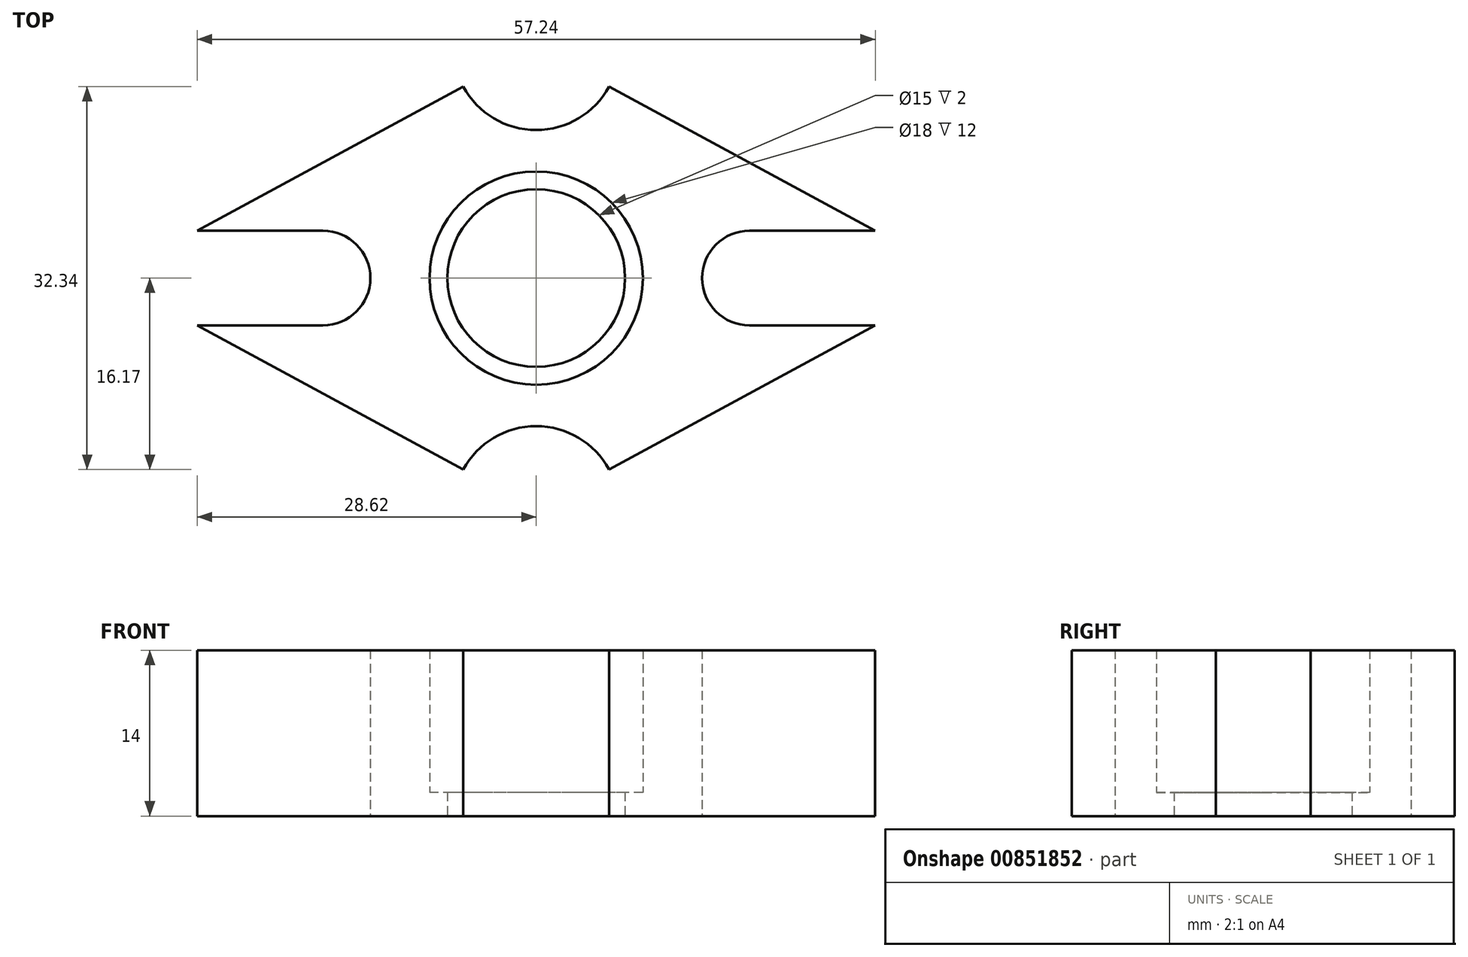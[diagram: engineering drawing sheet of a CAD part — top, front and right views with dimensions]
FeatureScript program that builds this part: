
annotation { "Feature Type Name" : "Feature", "Feature Type Description" : "" }
export const myFeature = defineFeature(function(context is Context, id is Id, definition is map)
    precondition{}
    {
        {
            var Q0;
            Q0=qCreatedBy(makeId("Top.planeOp"),FACE);
            var sketch = newSketch(context, id + "F0", { "sketchPlane" : qUnion([Q0])});
            skPoint(sketch, "E0.middle", {"position": v(0, 0) * mm});
            skCircle(sketch, "E1", {"center": v(0, 0) * mm, "radius": 7.5 * mm});
            skLineSegment(sketch, "E2", {"start": v(-6.16, 16.17) * mm, "end": v(-28.62, 4) * mm});
            skLineSegment(sketch, "E3", {"start": v(-28.62, -4) * mm, "end": v(-6.16, -16.17) * mm});
            skLineSegment(sketch, "E4", {"start": v(6.16, -16.17) * mm, "end": v(28.62, -4) * mm});
            skLineSegment(sketch, "E5", {"start": v(28.62, 4) * mm, "end": v(6.16, 16.17) * mm});
            skArc(sketch, "E6", {"start": v(-6.16, 16.17) * mm, "mid": v(0, 12.5) * mm, "end": v(6.16, 16.17) * mm});
            skArc(sketch, "E7", {"start": v(6.16, -16.17) * mm, "mid": v(0, -12.5) * mm, "end": v(-6.16, -16.17) * mm});
            skPoint(sketch, "E8.endSnap0", {"position": v(-18, 9.75) * mm});
            skPoint(sketch, "E9.orphan", {"position": v(36, -19.5) * mm});
            skPoint(sketch, "E10.orphan", {"position": v(-36, -19.5) * mm});
            skPoint(sketch, "E0.right.end.orphan", {"position": v(-36, 19.5) * mm});
            skPoint(sketch, "E0.left.end.orphan", {"position": v(36, 19.5) * mm});
            skArc(sketch, "E11.0.endCap", {"start": v(-18, 4) * mm, "mid": v(-14, 0) * mm, "end": v(-18, -4) * mm});
            skLineSegment(sketch, "E11.0.left", {"start": v(-28.62, 4) * mm, "end": v(-18, 4) * mm});
            skLineSegment(sketch, "E11.0.right", {"start": v(-28.62, -4) * mm, "end": v(-18, -4) * mm});
            skArc(sketch, "E11.1.endCap", {"start": v(18, -4) * mm, "mid": v(14, 0) * mm, "end": v(18, 4) * mm});
            skLineSegment(sketch, "E11.1.left", {"start": v(28.62, -4) * mm, "end": v(18, -4) * mm});
            skLineSegment(sketch, "E11.1.right", {"start": v(28.62, 4) * mm, "end": v(18, 4) * mm});
            skPoint(sketch, "E11.1.startCap.center.orphan", {"position": v(36, 0) * mm});
            skPoint(sketch, "E12.orphan", {"position": v(-36, 0) * mm});
            skCircle(sketch, "E13", {"center": v(0, 0) * mm, "radius": 9 * mm});
            skSolve(sketch);
        }
        {
            var Q0;
            Q0 = qSketchRegion(id + "F0", true);
            extrude(context, id + "F1", {"entities" : qUnion([Q0]), "depth" : 12 * mm, "offsetDistance" : 25 * mm});
        }
        {
            var Q0;
            Q0=makeQuery(id+"F1.opExtrude","CAP_FACE",FACE,{"disambiguationData":[OSD([sQuery(id+"F0.wireOp",EDGE,"E2"),sQuery(id+"F0.wireOp",EDGE,"E3"),sQuery(id+"F0.wireOp",EDGE,"E4"),sQuery(id+"F0.wireOp",EDGE,"E5"),sQuery(id+"F0.wireOp",EDGE,"E6"),sQuery(id+"F0.wireOp",EDGE,"E7"),sQuery(id+"F0.wireOp",EDGE,"E11.0.endCap"),sQuery(id+"F0.wireOp",EDGE,"E11.0.left"),sQuery(id+"F0.wireOp",EDGE,"E11.0.right"),sQuery(id+"F0.wireOp",EDGE,"E11.1.endCap"),sQuery(id+"F0.wireOp",EDGE,"E11.1.left"),sQuery(id+"F0.wireOp",EDGE,"E11.1.right"),sQuery(id+"F0.wireOp",EDGE,"E13")])],"isStart":false});
            var Q1;
            Q1=makeQuery(id+"F0.imprint","IMPRINT",FACE,{"disambiguationData":[TD([[makeQuery(id+"F0.imprint","IMPRINT",EDGE,{"derivedFrom":sQuery(id+"F0.wireOp",EDGE,"E1")}),-1.0]])]});
            extrude(context, id + "F2", {"entities" : qUnion([Q0, Q1]), "operationType" : NewBodyOperationType.ADD, "depth" : 2 * mm, "offsetDistance" : 25 * mm});
        }
    });
